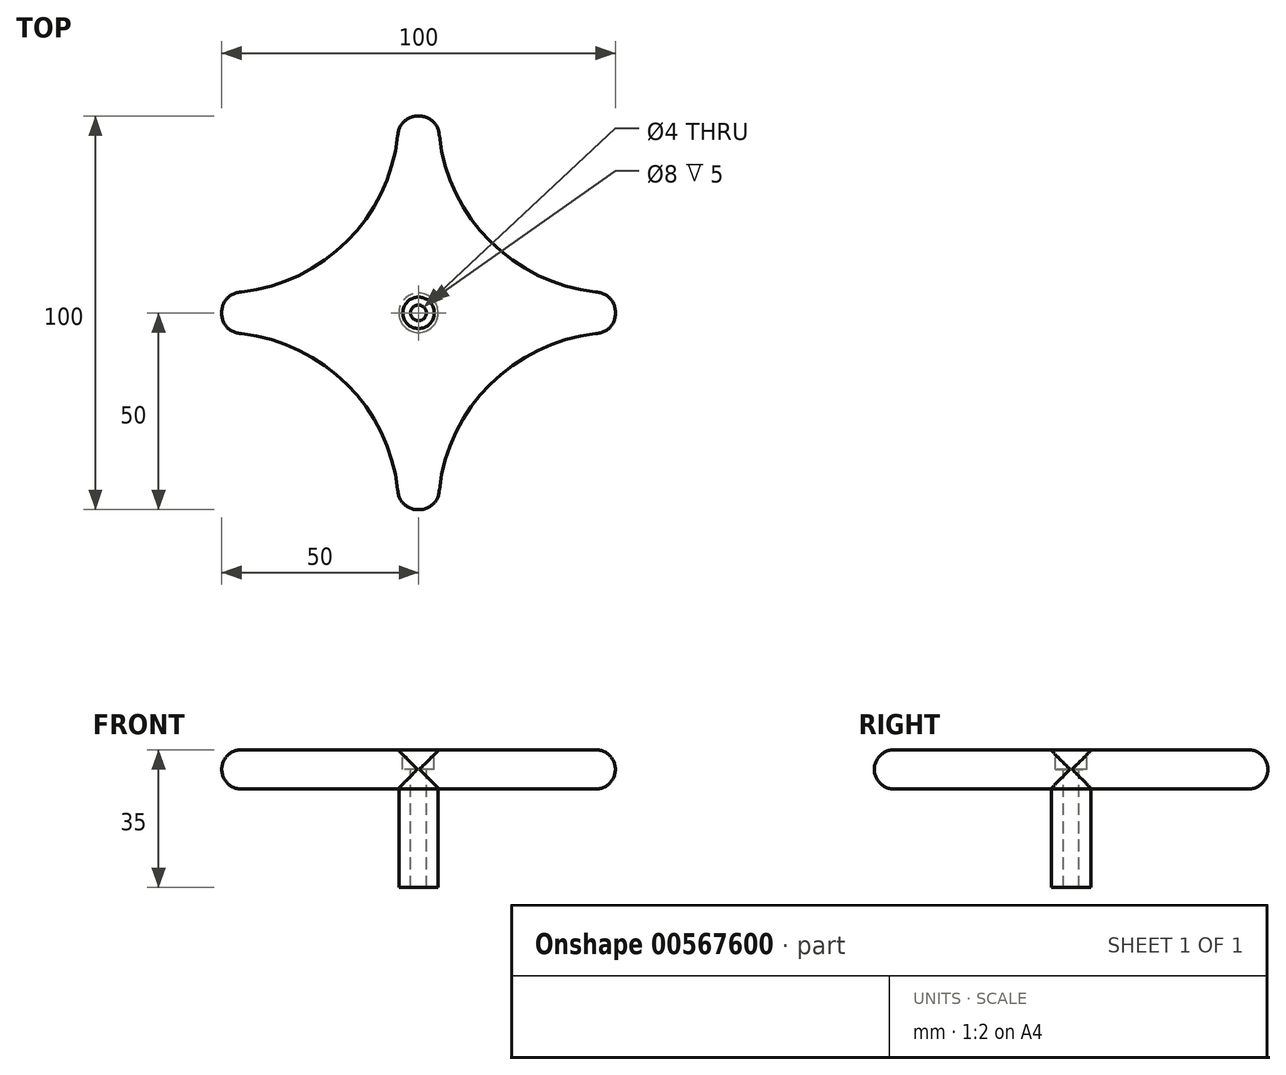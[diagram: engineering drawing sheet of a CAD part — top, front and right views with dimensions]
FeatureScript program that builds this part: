
annotation { "Feature Type Name" : "Feature", "Feature Type Description" : "" }
export const myFeature = defineFeature(function(context is Context, id is Id, definition is map)
    precondition{}
    {
        {
            var Q0;
            Q0=qCreatedBy(makeId("Top.planeOp"),FACE);
            var sketch = newSketch(context, id + "F0", { "sketchPlane" : qUnion([Q0])});
            skLineSegment(sketch, "E0.bottom", {"start": v(-50, -50) * mm, "end": v(50, -50) * mm});
            skLineSegment(sketch, "E0.top", {"start": v(-50, 50) * mm, "end": v(50, 50) * mm});
            skLineSegment(sketch, "E0.left", {"start": v(-50, -50) * mm, "end": v(-50, 50) * mm});
            skLineSegment(sketch, "E0.right", {"start": v(50, -50) * mm, "end": v(50, 50) * mm});
            skPoint(sketch, "E0.middle", {"position": v(0, 0) * mm});
            skCircle(sketch, "E1", {"center": v(-50, 50) * mm, "radius": 45 * mm});
            skCircle(sketch, "E2", {"center": v(50, 50) * mm, "radius": 45 * mm});
            skCircle(sketch, "E3", {"center": v(50, -50) * mm, "radius": 45 * mm});
            skCircle(sketch, "E4", {"center": v(-50, -50) * mm, "radius": 45 * mm});
            skSolve(sketch);
        }
        {
            var Q0;
            {var subQ5=sQuery(id+"F0.wireOp",EDGE,"E4");var subQ10=sQuery(id+"F0.wireOp",EDGE,"E0.bottom");var subQ11=makeQuery(id+"F0.imprint","INTERSECT",VERTEX,{"derivedFrom":[subQ10,subQ5]});Q0=makeQuery(id+"F0.imprint","IMPRINT",FACE,{"disambiguationData":[TD([[makeQuery(id+"F0.imprint","IMPRINT",EDGE,{"disambiguationData":[TD([[subQ11,-1.0]])],"derivedFrom":subQ10}),1.0]])]});}
            extrude(context, id + "F1", {"entities" : qUnion([Q0]), "depth" : 10 * mm, "offsetDistance" : 25 * mm});
        }
        {
            var Q0;
            Q0=makeQuery(id+"F1.opExtrude","CAP_FACE",FACE,{"disambiguationData":[OSD([sQuery(id+"F0.wireOp",EDGE,"E0.bottom"),sQuery(id+"F0.wireOp",EDGE,"E0.top"),sQuery(id+"F0.wireOp",EDGE,"E0.left"),sQuery(id+"F0.wireOp",EDGE,"E0.right"),sQuery(id+"F0.wireOp",EDGE,"E1"),sQuery(id+"F0.wireOp",EDGE,"E2"),sQuery(id+"F0.wireOp",EDGE,"E3"),sQuery(id+"F0.wireOp",EDGE,"E4")])],"isStart":false});
            var sketch = newSketch(context, id + "F2", { "sketchPlane" : qUnion([Q0])});
            skCircle(sketch, "E5", {"center": v(0, 0) * mm, "radius": 4 * mm});
            skCircle(sketch, "E6", {"center": v(0, 0) * mm, "radius": 2 * mm});
            skSolve(sketch);
        }
        {
            var Q0;
            Q0=makeQuery(id+"F2.imprint","IMPRINT",FACE,{"disambiguationData":[TD([[makeQuery(id+"F2.imprint","IMPRINT",EDGE,{"derivedFrom":sQuery(id+"F2.wireOp",EDGE,"E6")}),1.0]])]});
            var Q1;
            Q1=makeQuery(id+"F1.opExtrude","CAP_FACE",FACE,{"disambiguationData":[OSD([sQuery(id+"F0.wireOp",EDGE,"E0.bottom"),sQuery(id+"F0.wireOp",EDGE,"E0.top"),sQuery(id+"F0.wireOp",EDGE,"E0.left"),sQuery(id+"F0.wireOp",EDGE,"E0.right"),sQuery(id+"F0.wireOp",EDGE,"E1"),sQuery(id+"F0.wireOp",EDGE,"E2"),sQuery(id+"F0.wireOp",EDGE,"E3"),sQuery(id+"F0.wireOp",EDGE,"E4")])],"isStart":true});
            extrude(context, id + "F3", {"entities" : qUnion([Q0]), "operationType" : NewBodyOperationType.REMOVE, "endBound" : BoundingType.UP_TO_SURFACE, "oppositeDirection" : true, "depth" : 25 * mm, "endBoundEntityFace" : qUnion([Q1]), "offsetDistance" : 25 * mm});
        }
        {
            var Q0;
            Q0=makeQuery(id+"F2.imprint","IMPRINT",FACE,{"disambiguationData":[TD([[makeQuery(id+"F2.imprint","IMPRINT",EDGE,{"derivedFrom":sQuery(id+"F2.wireOp",EDGE,"E5")}),1.0]])]});
            extrude(context, id + "F4", {"entities" : qUnion([Q0]), "operationType" : NewBodyOperationType.REMOVE, "oppositeDirection" : true, "depth" : 5 * mm, "offsetDistance" : 25 * mm});
        }
        {
            var Q0;
            Q0=makeQuery(id+"F1.opExtrude","SWEPT_FACE",FACE,{"disambiguationData":[OSD([sQuery(id+"F0.wireOp",EDGE,"E0.top")])]});
            var Q1;
            Q1=makeQuery(id+"F1.opExtrude","SWEPT_FACE",FACE,{"disambiguationData":[OSD([sQuery(id+"F0.wireOp",EDGE,"E0.left")])]});
            var Q2;
            Q2=makeQuery(id+"F1.opExtrude","SWEPT_FACE",FACE,{"disambiguationData":[OSD([sQuery(id+"F0.wireOp",EDGE,"E0.bottom")])]});
            var Q3;
            Q3=makeQuery(id+"F1.opExtrude","SWEPT_FACE",FACE,{"disambiguationData":[OSD([sQuery(id+"F0.wireOp",EDGE,"E0.right")])]});
            fillet(context, id + "F5", {"entities" : qUnion([Q0, Q1, Q2, Q3]), "radius" : 5 * mm, "tangentPropagation" : true, "allowEdgeOverflow" : false});
        }
        {
            var Q0;
            Q0=makeQuery(id+"F1.opExtrude","CAP_FACE",FACE,{"disambiguationData":[OSD([sQuery(id+"F0.wireOp",EDGE,"E0.bottom"),sQuery(id+"F0.wireOp",EDGE,"E0.top"),sQuery(id+"F0.wireOp",EDGE,"E0.left"),sQuery(id+"F0.wireOp",EDGE,"E0.right"),sQuery(id+"F0.wireOp",EDGE,"E1"),sQuery(id+"F0.wireOp",EDGE,"E2"),sQuery(id+"F0.wireOp",EDGE,"E3"),sQuery(id+"F0.wireOp",EDGE,"E4")])],"isStart":true});
            var sketch = newSketch(context, id + "F6", { "sketchPlane" : qUnion([Q0])});
            skCircle(sketch, "E7", {"center": v(0, 0) * mm, "radius": 5 * mm});
            skSolve(sketch);
        }
        {
            var Q0;
            Q0=makeQuery(id+"F6.imprint","IMPRINT",FACE,{"disambiguationData":[TD([[makeQuery(id+"F6.imprint","IMPRINT",EDGE,{"derivedFrom":sQuery(id+"F6.wireOp",EDGE,"E7")}),1.0]])]});
            extrude(context, id + "F7", {"entities" : qUnion([Q0]), "operationType" : NewBodyOperationType.ADD, "depth" : 25 * mm, "offsetDistance" : 25 * mm});
        }
    });
